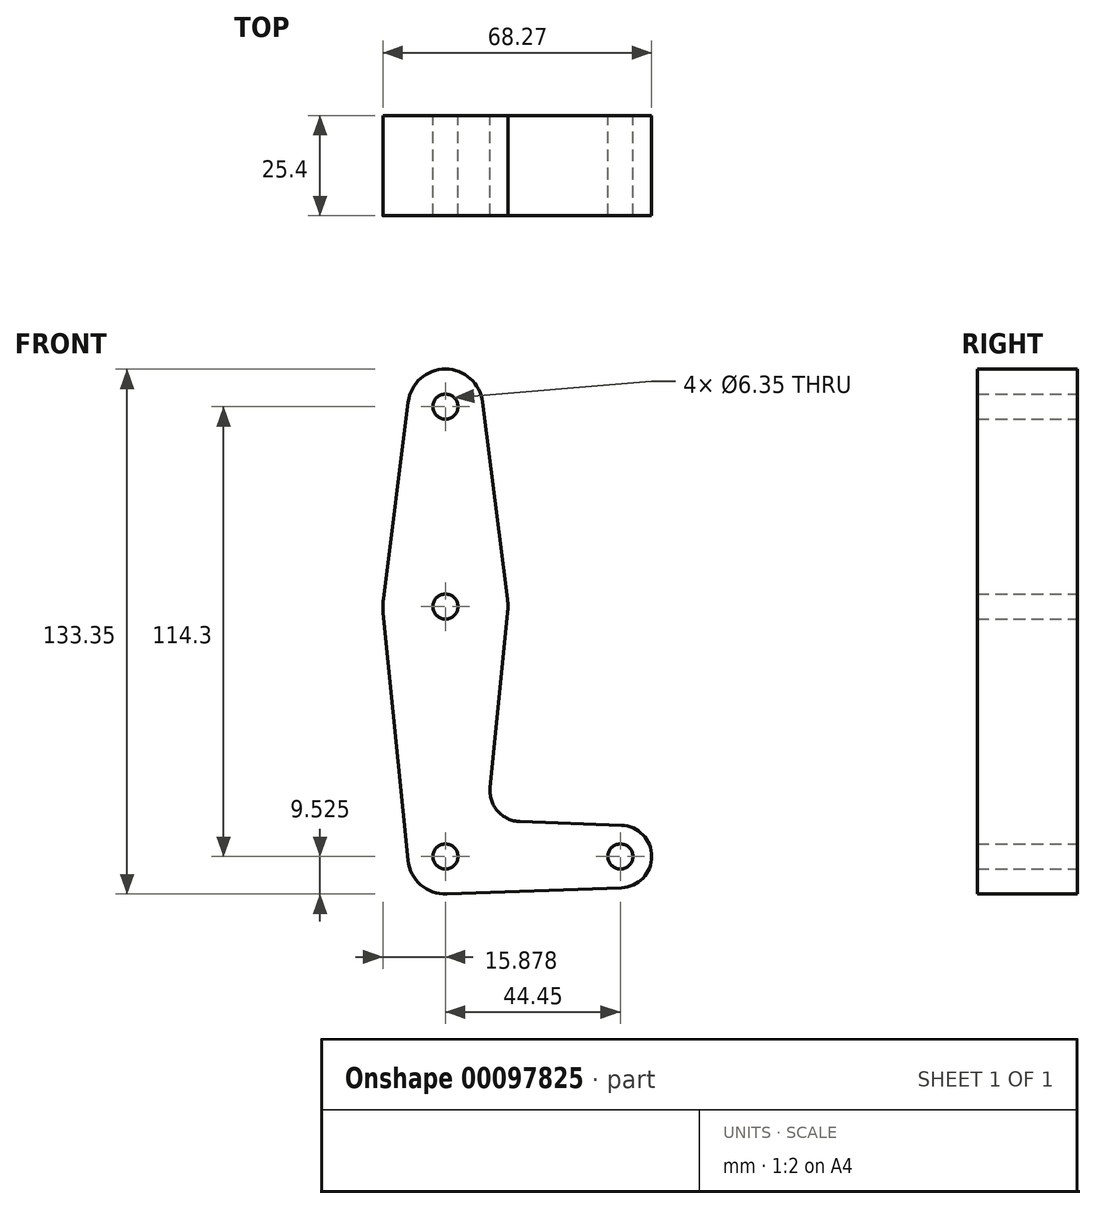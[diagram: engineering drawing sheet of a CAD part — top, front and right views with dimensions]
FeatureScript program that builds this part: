
annotation { "Feature Type Name" : "Feature", "Feature Type Description" : "" }
export const myFeature = defineFeature(function(context is Context, id is Id, definition is map)
    precondition{}
    {
        {
            var Q0;
            Q0=qCreatedBy(makeId("Front.planeOp"),FACE);
            var sketch = newSketch(context, id + "F0", { "sketchPlane" : qUnion([Q0])});
            skLineSegment(sketch, "E0", {"start": v(-31.66, 59.21) * mm, "end": v(-31.66, -55.09) * mm});
            skCircle(sketch, "E1", {"center": v(-31.66, 59.21) * mm, "radius": 9.53 * mm});
            skCircle(sketch, "E2", {"center": v(-31.66, 8.41) * mm, "radius": 15.88 * mm});
            skCircle(sketch, "E3", {"center": v(-31.66, -55.09) * mm, "radius": 9.53 * mm});
            skLineSegment(sketch, "E4", {"start": v(-31.66, -55.09) * mm, "end": v(12.79, -55.09) * mm});
            skCircle(sketch, "E5", {"center": v(12.79, -55.09) * mm, "radius": 7.94 * mm});
            skLineSegment(sketch, "E6", {"start": v(-22.21, 60.4) * mm, "end": v(-15.91, 10.4) * mm});
            skLineSegment(sketch, "E7", {"start": v(-41.11, 60.4) * mm, "end": v(-47.41, 10.4) * mm});
            skLineSegment(sketch, "E8", {"start": v(-15.87, 6.83) * mm, "end": v(-20.32, -37.5) * mm});
            skLineSegment(sketch, "E9", {"start": v(-47.46, 6.83) * mm, "end": v(-41.14, -56.04) * mm});
            skLineSegment(sketch, "E10", {"start": v(-31.32, -64.6) * mm, "end": v(13.07, -63.02) * mm});
            skCircle(sketch, "E11", {"center": v(-31.66, 59.21) * mm, "radius": 3.18 * mm});
            skCircle(sketch, "E12", {"center": v(-31.66, 8.41) * mm, "radius": 3.18 * mm});
            skCircle(sketch, "E13", {"center": v(-31.66, -55.09) * mm, "radius": 3.18 * mm});
            skLineSegment(sketch, "E14", {"start": v(-12.7, -46.23) * mm, "end": v(13.07, -47.15) * mm});
            skCircle(sketch, "E15", {"center": v(12.79, -55.09) * mm, "radius": 3.18 * mm});
            skArc(sketch, "E16.filletArc", {"start": v(-20.32, -37.5) * mm, "mid": v(-18.4, -43.51) * mm, "end": v(-12.7, -46.23) * mm});
            skSolve(sketch);
        }
        {
            var Q0;
            Q0 = qSketchRegion(id + "F0", true);
            var Q1;
            {var subQ0=sQuery(id+"F0.wireOp",EDGE,"E3");var subQ1=sQuery(id+"F0.wireOp",EDGE,"E0");var subQ2=makeQuery(id+"F0.imprint","INTERSECT",VERTEX,{"derivedFrom":[subQ1,subQ0]});Q1=makeQuery(id+"F0.imprint","IMPRINT",FACE,{"disambiguationData":[TD([[makeQuery(id+"F0.imprint","IMPRINT",EDGE,{"disambiguationData":[TD([[subQ2,-1.0]])],"derivedFrom":subQ1}),1.0]])]});}
            extrude(context, id + "F1", {"entities" : qUnion([Q0, Q1]), "depth" : 25.4 * mm});
        }
    });
